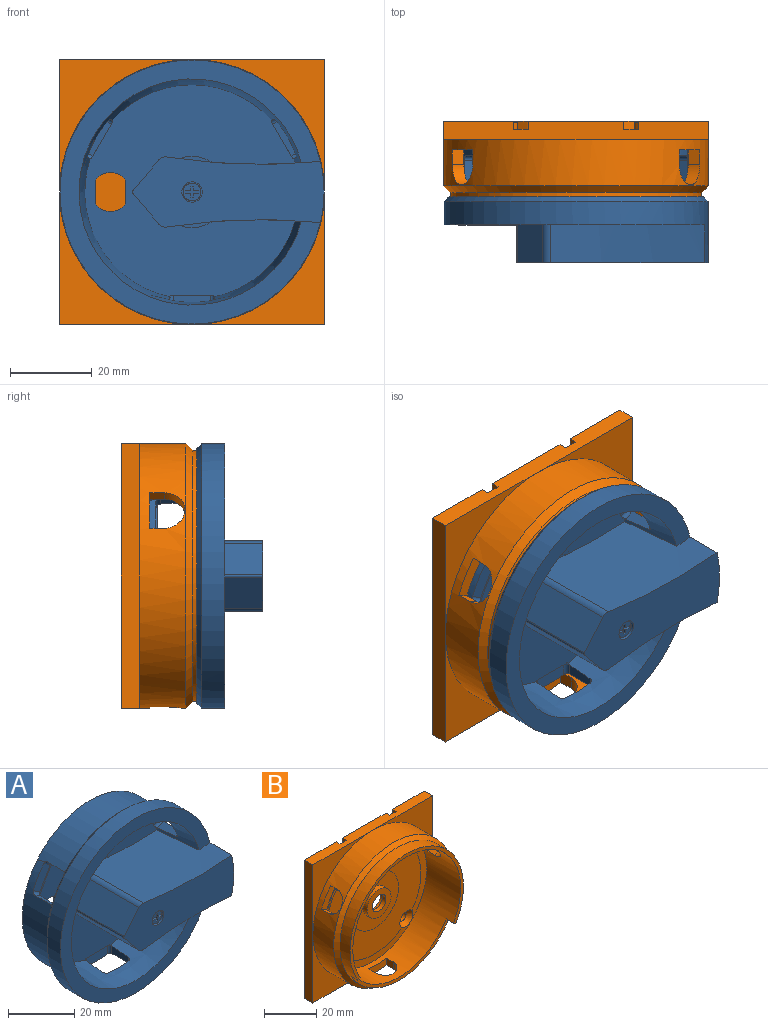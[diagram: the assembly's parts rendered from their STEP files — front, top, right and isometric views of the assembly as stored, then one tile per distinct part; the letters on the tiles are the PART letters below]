
ASSEMBLY  parts=2 mates=1
PART A: 88 faces, bbox 65.3x29.5x65.3 mm
  f0: cylinder r=1mm len=3.31mm, axis (-0.87,0,-0.5), area 4.8mm2, adj f2,f35,f39,f40,f68,f87
  f1: cylinder r=1mm len=2.47mm, axis (0.87,0,-0.5), area 3.2mm2, adj f2,f44,f50,f68
  f2: cylinder r=29.05mm len=58.1mm, axis (0,-1,0), area 3077.4mm2, adj f0,f1,f4,f7,f27,f28,f29,f30
  f3: plane 54x53.33mm, normal (0,1,0), area 1374.2mm2, adj f19,f20,f22,f23,f24,f25,f83,f84
  f4: plane 58.1x58.1mm, normal (0,1,0), area 354.3mm2, adj f2,f19,f20,f66,f84
  f5: plane 46.98x17.24mm, normal (0,-1,0), area 618.5mm2, adj f8,f9,f10,f11,f12,f13,f72,f78
  f6: plane 64.8x63.93mm, normal (0,-1,0), area 810.5mm2, adj f10,f11,f68,f81
  f7: plane 62.4x62.4mm, normal (0,1,0), area 407mm2, adj f2,f79
  f8: plane 25.8x7.58mm, normal (-0.77,0,-0.64), area 255.4mm2, adj f5,f9,f78,f87
  f9: cylinder r=2mm len=25.8mm, axis (0,1,0), area 53.2mm2, adj f5,f8,f10,f87
  f10: cylinder r=148.06mm len=37.78mm, axis (0,1,0), area 887.9mm2, adj f5,f6,f9,f68,f81,f87
  f11: cylinder r=148.06mm len=37.78mm, axis (0,1,0), area 887.9mm2, adj f5,f6,f12,f68,f81,f87
  f12: cylinder r=2mm len=25.8mm, axis (0,1,0), area 53.2mm2, adj f5,f11,f13,f87
  f13: plane 25.8x7.58mm, normal (-0.77,0,0.64), area 255.4mm2, adj f5,f12,f78,f87
  f14: plane 20.6x20.6mm, normal (0,1,0), area 37.7mm2, adj f67,f77,f82
  f15: plane 19.4x19.4mm, normal (0,1,0), area 55.1mm2, adj f76,f77
  f16: plane 17.5x17.5mm, normal (0,1,0), area 81mm2, adj f75,f76
  f17: plane 12x12mm, normal (0,1,0), area 14.6mm2, adj f74,f75
  f18: plane 9.5x9.5mm, normal (0,1,0), area 65.2mm2, adj f73,f85
  f19: plane 27.94x18.95mm, normal (0,0,1), area 494.2mm2, adj f3,f4,f21,f66,f67,f82,f83,f84
  f20: plane 27.95x18.97mm, normal (0,0,-1), area 494.3mm2, adj f3,f4,f21,f66,f67,f82,f83,f84
  f21: plane 19.18x12mm, normal (0,1,0), area 211.8mm2, adj f19,f20,f66,f67
  f22: cylinder r=4.75mm len=7.5mm, axis (0,1,0), area 23.3mm2, adj f3,f23,f25,f87
  f23: plane 5.83x2.7mm, normal (-1,0,0), area 15.7mm2, adj f3,f22,f24,f87
  f24: cylinder r=4.75mm len=7.5mm, axis (0,1,0), area 23.3mm2, adj f3,f23,f25,f87
  f25: plane 5.83x2.7mm, normal (1,0,0), area 15.7mm2, adj f3,f22,f24,f87
  f26: plane 10.6x0.4mm, normal (0,0,-1), area 4mm2, adj f29,f30,f31,f87
  f27: cylinder r=1mm len=2.28mm, axis (0,0,1), area 3.2mm2, adj f2,f28,f34,f68
  f28: plane 7.2x2.75mm, normal (1,0,0), area 17.5mm2, adj f2,f27,f29,f68
  f29: cylinder r=1mm len=3.25mm, axis (0,0,1), area 4.8mm2, adj f2,f26,f28,f30,f68,f87
  f30: plane 9x3.6mm, normal (0,-1,0), area 31.4mm2, adj f2,f26,f29,f31
  f31: cylinder r=1mm len=3.25mm, axis (0,0,1), area 4.8mm2, adj f2,f26,f30,f32,f68,f87
  f32: plane 7.2x2.75mm, normal (-1,0,0), area 17.5mm2, adj f2,f31,f33,f68
  f33: cylinder r=1mm len=2.28mm, axis (0,0,1), area 3.2mm2, adj f2,f32,f34,f68
  f34: plane 9x2.35mm, normal (0,1,0), area 17.8mm2, adj f2,f27,f33,f68
  f35: plane 9.18x5.3mm, normal (0.87,0,0.5), area 4mm2, adj f0,f40,f41,f87
  f36: cylinder r=1mm len=2.47mm, axis (-0.87,0,-0.5), area 3.2mm2, adj f2,f37,f42,f68
  f37: plane 8.79x6.23mm, normal (0,1,0), area 17.8mm2, adj f2,f36,f38,f68
  f38: cylinder r=1mm len=2.47mm, axis (-0.87,0,-0.5), area 3.2mm2, adj f2,f37,f39,f68
  f39: plane 7.2x2.38mm, normal (-0.5,0,0.87), area 17.5mm2, adj f0,f2,f38,f68
  f40: plane 9.42x7.31mm, normal (0,-1,0), area 31.4mm2, adj f0,f2,f35,f41
  f41: cylinder r=1mm len=3.31mm, axis (-0.87,0,-0.5), area 4.8mm2, adj f2,f35,f40,f42,f68,f87
  f42: plane 7.2x2.38mm, normal (0.5,0,-0.87), area 17.5mm2, adj f2,f36,f41,f68
  f43: plane 9.18x5.3mm, normal (-0.87,0,0.5), area 4mm2, adj f47,f48,f49,f87
  f44: plane 8.79x6.23mm, normal (0,1,0), area 17.8mm2, adj f1,f2,f45,f68
  f45: cylinder r=1mm len=2.47mm, axis (0.87,0,-0.5), area 3.2mm2, adj f2,f44,f46,f68
  f46: plane 7.2x2.38mm, normal (-0.5,0,-0.87), area 17.5mm2, adj f2,f45,f47,f68
  f47: cylinder r=1mm len=3.31mm, axis (0.87,0,-0.5), area 4.8mm2, adj f2,f43,f46,f48,f68,f87
  f48: plane 9.42x7.31mm, normal (0,-1,0), area 31.4mm2, adj f2,f43,f47,f49
  f49: cylinder r=1mm len=3.31mm, axis (0.87,0,-0.5), area 4.8mm2, adj f2,f43,f48,f50,f68,f87
  f50: plane 7.2x2.38mm, normal (0.5,0,0.87), area 17.5mm2, adj f1,f2,f49,f68
  f51: plane 4.38x4.38mm, normal (0,-1,0), area 11.4mm2, adj f54,f55,f56,f57,f58,f59,f60,f61
  f52: plane 2.5x2.5mm, normal (0,1,0), area 4.9mm2, adj f70
  f53: plane 2.7x2.7mm, normal (0,1,0), area 0.8mm2, adj f70,f85
  f54: plane 1.66x0.75mm, normal (0,0,-1), area 1.2mm2, adj f51,f55,f64,f65
  f55: plane 0.94x0.75mm, normal (1,0,0), area 0.7mm2, adj f51,f54,f56,f64
  f56: plane 0.75x0.63mm, normal (0,0,-1), area 0.5mm2, adj f51,f55,f57,f64
  f57: plane 0.94x0.75mm, normal (-1,0,0), area 0.7mm2, adj f51,f56,f58,f64
  f58: plane 1.66x0.75mm, normal (0,0,-1), area 1.2mm2, adj f51,f57,f64,f69
  f59: plane 1.66x0.75mm, normal (0,0,1), area 1.2mm2, adj f51,f60,f64,f69
  f60: plane 0.94x0.75mm, normal (-1,0,0), area 0.7mm2, adj f51,f59,f61,f64
  f61: plane 0.75x0.63mm, normal (0,0,1), area 0.5mm2, adj f51,f60,f62,f64
  f62: plane 0.94x0.75mm, normal (1,0,0), area 0.7mm2, adj f51,f61,f63,f64
  f63: plane 1.66x0.75mm, normal (0,0,1), area 1.2mm2, adj f51,f62,f64,f65
  f64: plane 4x2.5mm, normal (0,-1,0), area 3.7mm2, adj f54,f55,f56,f57,f58,f59,f60,f61
  f65: cylinder r=2mm len=0.75mm, axis (0,-1,0), area 0.5mm2, adj f51,f54,f63,f64
  f66: cylinder r=27.55mm len=27.5mm, axis (0,1,0), area 332.7mm2, adj f4,f19,f20,f21
  f67: cylinder r=10.3mm len=24.5mm, axis (0,1,0), area 313.8mm2, adj f14,f19,f20,f21
  f68: cone r=27.75mm half-angle=5deg, axis (0,-1,0), area 2286.5mm2, adj f0,f1,f6,f10,f11,f27,f28,f29
  f69: cylinder r=2mm len=0.75mm, axis (0,-1,0), area 0.5mm2, adj f51,f58,f59,f64
  f70: cylinder r=1.25mm len=10mm, axis (0,1,0), area 78.5mm2, adj f52,f53
  f71: cylinder r=2.19mm len=4.38mm, axis (0,1,0), area 17.4mm2, adj f51,f86
  f72: cylinder r=2.5mm len=5mm, axis (0,1,0), area 26.7mm2, adj f5,f86
  f73: cylinder r=4.75mm len=14.33mm, axis (0,1,0), area 427.6mm2, adj f18,f74
  f74: cone r=4.75mm half-angle=15deg, axis (0,1,0), area 106.8mm2, adj f17,f73
  f75: cone r=6mm half-angle=15deg, axis (0,1,0), area 179.3mm2, adj f16,f17
  f76: cylinder r=8.75mm len=17.5mm, axis (0,1,0), area 110mm2, adj f15,f16
  f77: cylinder r=9.7mm len=19.4mm, axis (0,1,0), area 115.8mm2, adj f14,f15
  f78: cylinder r=0.5mm len=25.8mm, axis (0,1,0), area 18mm2, adj f5,f8,f13,f87
  f79: cylinder r=31.2mm len=62.4mm, axis (0,-1,0), area 1117.4mm2, adj f7,f80
  f80: cone r=31.2mm half-angle=45deg, axis (0,-1,0), area 339.1mm2, adj f79,f81
  f81: cylinder r=32.4mm len=64.8mm, axis (0,-1,0), area 1300.6mm2, adj f5,f6,f10,f11,f80
  f82: cone r=10.3mm half-angle=35deg, axis (0,1,0), area 29.6mm2, adj f14,f19,f20,f83
  f83: cone r=10.62mm half-angle=65deg, axis (0,1,0), area 327mm2, adj f3,f19,f20,f82
  f84: cylinder r=27mm len=54mm, axis (0,1,0), area 78.8mm2, adj f3,f4,f19,f20
  f85: cylinder r=1.35mm len=2.7mm, axis (0,1,0), area 18.7mm2, adj f18,f53
  f86: plane 5x5mm, normal (0,-1,0), area 4.6mm2, adj f71,f72
  f87: plane 52.07x51.67mm, normal (0,-1,0), area 1540.3mm2, adj f0,f8,f9,f10,f11,f12,f13,f22
PART B: 110 faces, bbox 65x23x65 mm
  f0: cylinder r=32.5mm len=65mm, axis (0,-1,0), area 2094.4mm2, adj f2,f3,f13,f15,f62,f63,f64,f65
  f1: cylinder r=29.3mm len=58.6mm, axis (0,-1,0), area 2947.1mm2, adj f2,f3,f15,f58,f69,f76,f77,f78
  f2: cylinder r=5mm len=10.28mm, axis (-0.87,0,0.5), area 50.9mm2, adj f0,f1,f86,f87
  f3: cylinder r=5mm len=10mm, axis (0,0,1), area 50.6mm2, adj f0,f1,f80,f81
  f4: cylinder r=17.2mm len=34.4mm, axis (0,-1,0), area 259.4mm2, adj f56,f75
  f5: cylinder r=12mm len=24mm, axis (0,-1,0), area 143.3mm2, adj f74,f75
  f6: cone r=2.05mm half-angle=45deg, axis (0,-1,0), area 48.9mm2, adj f11,f35,f58
  f7: cylinder r=4mm len=7.66mm, axis (0,-1,0), area 43.4mm2, adj f18,f50,f93,f104
  f8: cylinder r=4mm len=7.66mm, axis (0,-1,0), area 43.4mm2, adj f18,f47,f92,f104
  f9: plane 65x4.5mm, normal (-1,0,0), area 292.5mm2, adj f45,f63,f64,f66,f67
  f10: plane 13x13mm, normal (0,-1,0), area 89.7mm2, adj f39,f41
  f11: cylinder r=3.9mm len=6.51mm, axis (0,-1,0), area 8.3mm2, adj f6,f43,f59,f61
  f12: plane 45.4x45.4mm, normal (0,1,0), area 424.2mm2, adj f26,f44
  f13: cone r=32.5mm half-angle=45deg, axis (0,1,0), area 478.1mm2, adj f0,f42
  f14: plane 2.25x1.5mm, normal (1,0,0), area 3.4mm2, adj f45,f67,f90,f105
  f15: cylinder r=5mm len=10.28mm, axis (0.87,0,0.5), area 50.9mm2, adj f0,f1,f83,f84
  f16: cylinder r=4mm len=1.68mm, axis (0,-1,0), area 0.3mm2, adj f44,f49,f54,f93
  f17: cylinder r=4mm len=1.68mm, axis (0,-1,0), area 0.3mm2, adj f44,f48,f52,f92
  f18: cylinder r=24.25mm len=28.61mm, axis (0,-1,0), area 91.8mm2, adj f7,f8,f55,f94,f97,f104
  f19: cylinder r=3.9mm len=6.51mm, axis (0,-1,0), area 8.3mm2, adj f34,f43,f59,f60
  f20: cylinder r=25.5mm len=30.13mm, axis (0,-1,0), area 22.6mm2, adj f29,f32,f58,f59
  f21: cylinder r=4mm len=7.66mm, axis (0,-1,0), area 43.4mm2, adj f25,f49,f93,f104
  f22: cylinder r=4mm len=7.66mm, axis (0,-1,0), area 43.4mm2, adj f25,f48,f92,f104
  f23: cylinder r=4mm len=1.68mm, axis (0,-1,0), area 0.3mm2, adj f44,f50,f54,f93
  f24: cylinder r=4mm len=1.68mm, axis (0,-1,0), area 0.3mm2, adj f44,f47,f52,f92
  f25: cylinder r=24.25mm len=28.61mm, axis (0,-1,0), area 91.8mm2, adj f21,f22,f53,f95,f96,f104
  f26: cylinder r=19.5mm len=39mm, axis (0,-1,0), area 220.5mm2, adj f12,f56
  f27: cylinder r=2.05mm len=4.1mm, axis (0,-1,0), area 31.6mm2, adj f28,f50
  f28: cone r=2.05mm half-angle=45deg, axis (0,-1,0), area 48.9mm2, adj f27,f29,f58
  f29: cylinder r=3.9mm len=6.51mm, axis (0,-1,0), area 8.3mm2, adj f20,f28,f59,f60
  f30: cylinder r=2.05mm len=4.1mm, axis (0,-1,0), area 31.6mm2, adj f31,f47
  f31: cone r=2.05mm half-angle=45deg, axis (0,-1,0), area 48.9mm2, adj f30,f32,f58
  f32: cylinder r=3.9mm len=6.51mm, axis (0,-1,0), area 8.3mm2, adj f20,f31,f59,f61
  f33: cylinder r=2.05mm len=4.1mm, axis (0,-1,0), area 31.6mm2, adj f34,f49
  f34: cone r=2.05mm half-angle=45deg, axis (0,-1,0), area 48.9mm2, adj f19,f33,f58
  f35: cylinder r=2.05mm len=4.1mm, axis (0,-1,0), area 31.6mm2, adj f6,f48
  f36: cylinder r=9.25mm len=18.5mm, axis (0,-1,0), area 110.4mm2, adj f73,f74
  f37: cylinder r=7.6mm len=15.2mm, axis (0,-1,0), area 90.7mm2, adj f72,f73
  f38: cylinder r=4.5mm len=9mm, axis (0,-1,0), area 48.1mm2, adj f71,f72
  f39: cylinder r=3.7mm len=7.4mm, axis (0,-1,0), area 46.5mm2, adj f10,f71
  f40: cylinder r=12.85mm len=25.7mm, axis (0,-1,0), area 40.4mm2, adj f59,f70
  f41: cylinder r=6.5mm len=13mm, axis (0,-1,0), area 93.9mm2, adj f10,f70
  f42: cylinder r=30.8mm len=61.6mm, axis (0,-1,0), area 806.3mm2, adj f13,f69,f76,f77,f78
  f43: cylinder r=25.5mm len=30.13mm, axis (0,-1,0), area 22.6mm2, adj f11,f19,f58,f59
  f44: cylinder r=22.7mm len=45.4mm, axis (0,-1,0), area 252.3mm2, adj f12,f16,f17,f23,f24,f47,f48,f49
  f45: plane 65x22.25mm, normal (0,1,0), area 152.3mm2, adj f9,f14,f66,f67,f88,f90,f91,f99
  f46: plane 10.5x1.5mm, normal (0,1,0), area 15.8mm2, adj f67,f90,f106,f107
  f47: plane 8x8mm, normal (0,1,0), area 32.1mm2, adj f8,f24,f30,f44,f94
  f48: plane 8x8mm, normal (0,1,0), area 32.1mm2, adj f17,f22,f35,f44,f95
  f49: plane 8x8mm, normal (0,1,0), area 32.1mm2, adj f16,f21,f33,f44,f96
  f50: plane 8x8mm, normal (0,1,0), area 32.1mm2, adj f7,f23,f27,f44,f97
  f51: plane 65x22.25mm, normal (0,1,0), area 152.3mm2, adj f66,f67,f68,f88,f89,f90,f102,f108
  f52: plane 28.61x6.35mm, normal (0,1,0), area 46.8mm2, adj f17,f24,f44,f92
  f53: plane 28.61x6.35mm, normal (0,1,0), area 46.8mm2, adj f25,f44,f95,f96
  f54: plane 28.61x6.35mm, normal (0,1,0), area 46.8mm2, adj f16,f23,f44,f93
  f55: plane 28.61x6.35mm, normal (0,1,0), area 46.8mm2, adj f18,f44,f94,f97
  f56: plane 39x39mm, normal (0,1,0), area 265.2mm2, adj f4,f26
  f57: plane 23.5x1.5mm, normal (0,1,0), area 35.3mm2, adj f66,f88,f98,f103
  f58: plane 58.6x58.6mm, normal (0,-1,0), area 558.6mm2, adj f1,f6,f20,f28,f31,f34,f43,f60
  f59: plane 51x51mm, normal (0,-1,0), area 1428.5mm2, adj f11,f19,f20,f29,f32,f40,f43,f60
  f60: cylinder r=25.5mm len=30.13mm, axis (0,-1,0), area 22.6mm2, adj f19,f29,f58,f59
  f61: cylinder r=25.5mm len=30.13mm, axis (0,-1,0), area 22.6mm2, adj f11,f32,f58,f59
  f62: plane 32.5x32.5mm, normal (0,-1,0), area 226.7mm2, adj f0,f67,f68
  f63: plane 32.5x32.5mm, normal (0,-1,0), area 226.7mm2, adj f0,f9,f67
  f64: plane 32.5x32.5mm, normal (0,-1,0), area 226.7mm2, adj f0,f9,f66
  f65: plane 32.5x32.5mm, normal (0,-1,0), area 226.7mm2, adj f0,f66,f68
  f66: plane 65x4.5mm, normal (0,0,1), area 278.5mm2, adj f9,f45,f51,f57,f64,f65,f68,f98
  f67: plane 65x4.5mm, normal (0,0,-1), area 270mm2, adj f9,f14,f45,f46,f51,f62,f63,f68
  f68: plane 65x4.5mm, normal (1,0,0), area 292.5mm2, adj f51,f62,f65,f66,f67
  f69: plane 61.6x46.2mm, normal (0,-1,0), area 188.8mm2, adj f1,f42,f77,f78
  f70: plane 25.7x25.7mm, normal (0,-1,0), area 386mm2, adj f40,f41
  f71: plane 9x9mm, normal (0,1,0), area 20.6mm2, adj f38,f39
  f72: plane 15.2x15.2mm, normal (0,1,0), area 117.8mm2, adj f37,f38
  f73: plane 18.5x18.5mm, normal (0,1,0), area 87.3mm2, adj f36,f37
  f74: plane 24x24mm, normal (0,1,0), area 183.6mm2, adj f5,f36
  f75: plane 34.4x34.4mm, normal (0,1,0), area 477mm2, adj f4,f5
  f76: plane 53.35x16.15mm, normal (0,-1,0), area 94.4mm2, adj f1,f42,f77,f78
  f77: plane 4x1.3mm, normal (-0.5,0,-0.87), area 6mm2, adj f1,f42,f69,f76
  f78: plane 4x1.3mm, normal (0.5,0,-0.87), area 6mm2, adj f1,f42,f69,f76
  f79: plane 10x3.63mm, normal (0,-1,0), area 32.1mm2, adj f0,f1,f80,f81
  f80: plane 3.63x3.24mm, normal (-1,0,0), area 11.8mm2, adj f0,f1,f3,f79
  f81: plane 3.63x3.24mm, normal (1,0,0), area 11.8mm2, adj f0,f1,f3,f79
  f82: plane 10.28x7.81mm, normal (0,-1,0), area 32.1mm2, adj f0,f1,f83,f84
  f83: plane 3.63x2.81mm, normal (-0.5,0,0.87), area 11.8mm2, adj f0,f1,f15,f82
  f84: plane 3.63x2.81mm, normal (0.5,0,-0.87), area 11.8mm2, adj f0,f1,f15,f82
  f85: plane 10.28x7.81mm, normal (0,-1,0), area 32.1mm2, adj f0,f1,f86,f87
  f86: plane 3.63x2.81mm, normal (-0.5,0,-0.87), area 11.8mm2, adj f0,f1,f2,f85
  f87: plane 3.63x2.81mm, normal (0.5,0,0.87), area 11.8mm2, adj f0,f1,f2,f85
  f88: plane 62x3mm, normal (0,0,-1), area 172mm2, adj f45,f51,f57,f89,f91,f98,f99,f100
  f89: plane 62x3mm, normal (-1,0,0), area 186mm2, adj f51,f88,f90,f104
  f90: plane 62x3mm, normal (0,0,1), area 163.5mm2, adj f14,f45,f46,f51,f89,f91,f104,f105
  f91: plane 62x3mm, normal (1,0,0), area 186mm2, adj f45,f88,f90,f104
  f92: cylinder r=24.25mm len=28.61mm, axis (0,-1,0), area 91.8mm2, adj f8,f17,f22,f24,f52,f104
  f93: cylinder r=24.25mm len=28.61mm, axis (0,-1,0), area 91.8mm2, adj f7,f16,f21,f23,f54,f104
  f94: cylinder r=4mm len=1.68mm, axis (0,-1,0), area 0.3mm2, adj f18,f44,f47,f55
  f95: cylinder r=4mm len=1.68mm, axis (0,-1,0), area 0.3mm2, adj f25,f44,f48,f53
  f96: cylinder r=4mm len=1.68mm, axis (0,-1,0), area 0.3mm2, adj f25,f44,f49,f53
  f97: cylinder r=4mm len=1.68mm, axis (0,-1,0), area 0.3mm2, adj f18,f44,f50,f55
  f98: plane 2x1.5mm, normal (-1,0,0), area 3mm2, adj f57,f66,f88,f100
  f99: plane 2x1.5mm, normal (1,0,0), area 3mm2, adj f45,f66,f88,f100
  f100: plane 3.5x1.5mm, normal (0,1,0), area 5.3mm2, adj f66,f88,f98,f99
  f101: plane 3.5x1.5mm, normal (0,1,0), area 5.3mm2, adj f66,f88,f102,f103
  f102: plane 2x1.5mm, normal (-1,0,0), area 3mm2, adj f51,f66,f88,f101
  f103: plane 2x1.5mm, normal (1,0,0), area 3mm2, adj f57,f66,f88,f101
  f104: plane 62x62mm, normal (0,1,0), area 1856.7mm2, adj f7,f8,f18,f21,f22,f25,f88,f89
  f105: plane 5x1.5mm, normal (0,1,0), area 7.5mm2, adj f14,f67,f90,f106
  f106: plane 2.25x1.5mm, normal (-1,0,0), area 3.4mm2, adj f46,f67,f90,f105
  f107: plane 2.25x1.5mm, normal (1,0,0), area 3.4mm2, adj f46,f67,f90,f109
  f108: plane 2.25x1.5mm, normal (-1,0,0), area 3.4mm2, adj f51,f67,f90,f109
  f109: plane 5x1.5mm, normal (0,1,0), area 7.5mm2, adj f67,f90,f107,f108
PLACE A t=(-141.91,-211.56,77.88)mm
PLACE B t=(-141.91,-211.86,77.88)mm
MATE fastened A.f2 <-> B.f0  axis (0,1,0) through (-141.91,-297.36,77.88)mm
